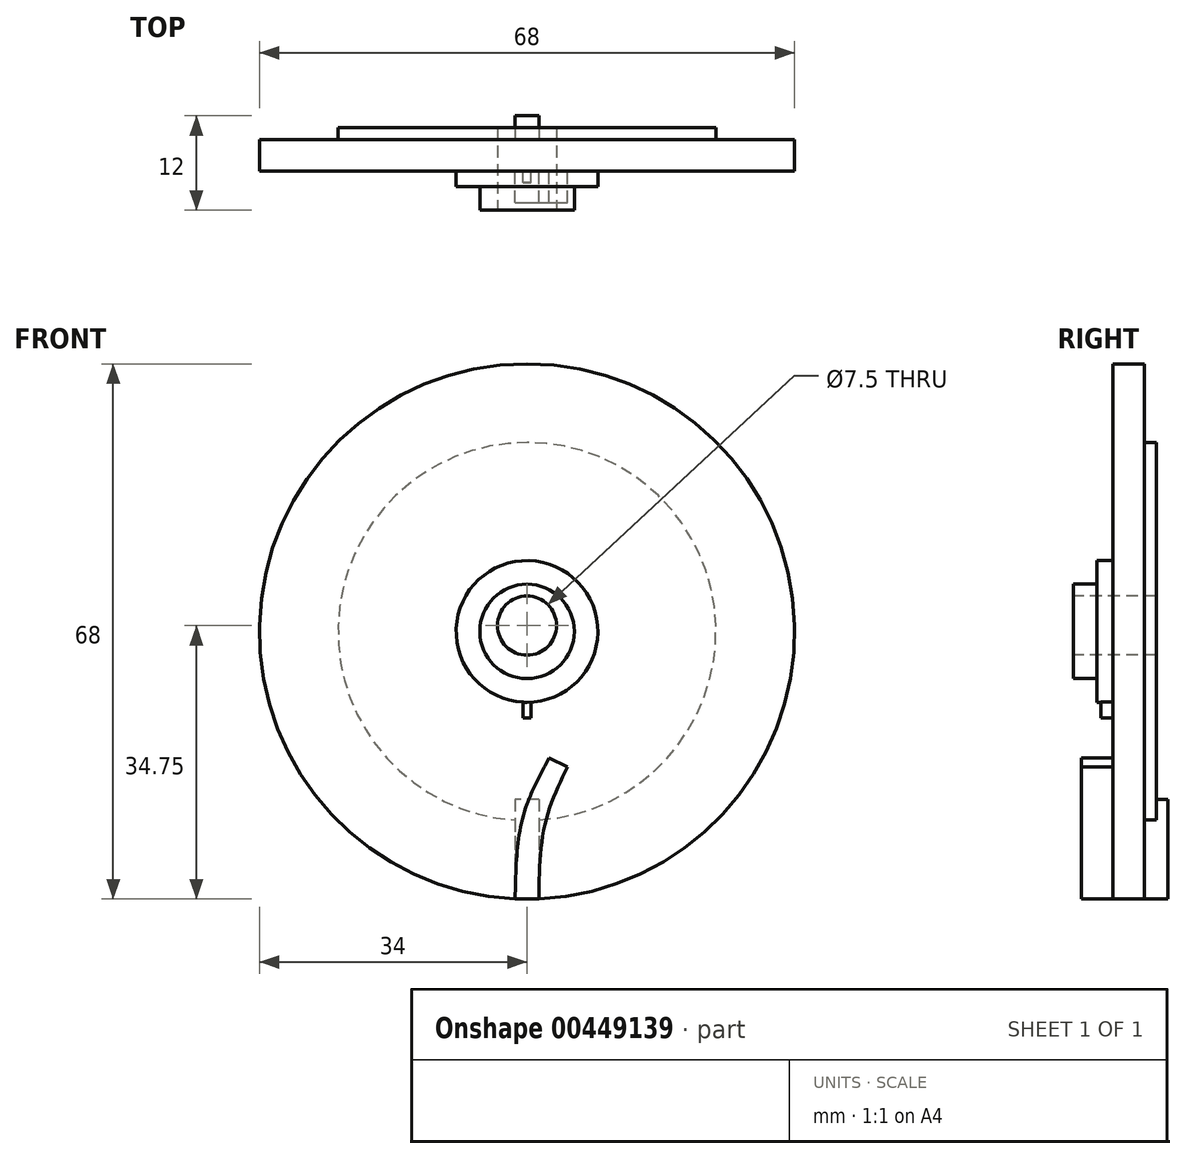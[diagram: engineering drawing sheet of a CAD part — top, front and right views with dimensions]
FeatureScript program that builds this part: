
annotation { "Feature Type Name" : "Feature", "Feature Type Description" : "" }
export const myFeature = defineFeature(function(context is Context, id is Id, definition is map)
    precondition{}
    {
        {
            var Q0;
            Q0=qCreatedBy(makeId("Front.planeOp"),FACE);
            var sketch = newSketch(context, id + "F0", { "sketchPlane" : qUnion([Q0])});
            skCircle(sketch, "E0", {"center": v(0, 0) * mm, "radius": 34 * mm});
            skSolve(sketch);
        }
        {
            var Q0;
            Q0=makeQuery(id+"F0.imprint","IMPRINT",FACE,{"disambiguationData":[TD([[makeQuery(id+"F0.imprint","IMPRINT",EDGE,{"derivedFrom":sQuery(id+"F0.wireOp",EDGE,"E0")}),1.0]])]});
            extrude(context, id + "F1", {"entities" : qUnion([Q0]), "depth" : 4 * mm});
        }
        {
            var Q0;
            Q0=qCreatedBy(makeId("Front.planeOp"),FACE);
            var sketch = newSketch(context, id + "F2", { "sketchPlane" : qUnion([Q0])});
            skCircle(sketch, "E1", {"center": v(0, 0) * mm, "radius": 6 * mm});
            skSolve(sketch);
        }
        {
            var Q0;
            Q0=qCreatedBy(makeId("Front.planeOp"),FACE);
            var sketch = newSketch(context, id + "F3", { "sketchPlane" : qUnion([Q0])});
            skCircle(sketch, "E2", {"center": v(0, 0) * mm, "radius": 24 * mm});
            skSolve(sketch);
        }
        {
            var Q0;
            Q0=qCreatedBy(makeId("Front.planeOp"),FACE);
            var sketch = newSketch(context, id + "F4", { "sketchPlane" : qUnion([Q0])});
            skCircle(sketch, "E3", {"center": v(0, 0) * mm, "radius": 9 * mm});
            skSolve(sketch);
        }
        {
            var Q0;
            Q0=qCreatedBy(makeId("Front.planeOp"),FACE);
            var sketch = newSketch(context, id + "F5", { "sketchPlane" : qUnion([Q0])});
            skLineSegment(sketch, "E4.bottom", {"start": v(1.53, -21.36) * mm, "end": v(-1.53, -21.36) * mm});
            skLineSegment(sketch, "E4.left", {"start": v(1.53, -21.36) * mm, "end": v(1.53, -33.97) * mm});
            skLineSegment(sketch, "E4.right", {"start": v(-1.53, -21.36) * mm, "end": v(-1.53, -33.97) * mm});
            skPoint(sketch, "E4.middle", {"position": v(0, -34) * mm});
            skArc(sketch, "E5", {"start": v(-1.53, -33.97) * mm, "mid": v(0, -34) * mm, "end": v(1.53, -33.97) * mm});
            skPoint(sketch, "E4.top.end.orphan", {"position": v(-1.53, -46.64) * mm});
            skPoint(sketch, "E4.top.start.orphan", {"position": v(1.53, -46.64) * mm});
            skSolve(sketch);
        }
        {
            var Q0;
            Q0 = qSketchRegion(id + "F2", true);
            extrude(context, id + "F6", {"entities" : qUnion([Q0]), "operationType" : NewBodyOperationType.ADD, "depth" : 9 * mm});
        }
        {
            var Q0;
            Q0 = qSketchRegion(id + "F4", true);
            extrude(context, id + "F7", {"entities" : qUnion([Q0]), "operationType" : NewBodyOperationType.ADD, "depth" : 6 * mm});
        }
        {
            var Q0;
            Q0 = qSketchRegion(id + "F3", true);
            extrude(context, id + "F8", {"entities" : qUnion([Q0]), "operationType" : NewBodyOperationType.ADD, "oppositeDirection" : true, "depth" : 1.5 * mm});
        }
        {
            var Q0;
            Q0 = qSketchRegion(id + "F5", true);
            extrude(context, id + "F9", {"entities" : qUnion([Q0]), "operationType" : NewBodyOperationType.ADD, "oppositeDirection" : true, "depth" : 3 * mm});
        }
        {
            var Q0;
            Q0=qCreatedBy(makeId("Right.planeOp"),FACE);
            var sketch = newSketch(context, id + "F10", { "sketchPlane" : qUnion([Q0])});
            skLineSegment(sketch, "E6", {"start": v(0, 0) * mm, "end": v(30, 0) * mm});
            skSolve(sketch);
        }
        {
            var Q0;
            Q0=qCreatedBy(makeId("Front.planeOp"),FACE);
            var sketch = newSketch(context, id + "F11", { "sketchPlane" : qUnion([Q0])});
            skLineSegment(sketch, "E7", {"start": v(0, 0) * mm, "end": v(0, 0.75) * mm});
            skCircle(sketch, "E8", {"center": v(0, 0.75) * mm, "radius": 3.75 * mm});
            skSolve(sketch);
        }
        {
            var Q0;
            Q0 = qSketchRegion(id + "F11", true);
            extrude(context, id + "F12", {"entities" : qUnion([Q0]), "operationType" : NewBodyOperationType.REMOVE, "endBound" : BoundingType.THROUGH_ALL, "oppositeDirection" : true, "depth" : 25 * mm});
        }
        {
            var Q0;
            Q0 = qSketchRegion(id + "F11", true);
            extrude(context, id + "F13", {"entities" : qUnion([Q0]), "operationType" : NewBodyOperationType.REMOVE, "endBound" : BoundingType.THROUGH_ALL, "depth" : 25 * mm});
        }
        {
            var Q0;
            Q0=qCreatedBy(makeId("Front.planeOp"),FACE);
            var sketch = newSketch(context, id + "F14", { "sketchPlane" : qUnion([Q0])});
            skLineSegment(sketch, "E9.bottom", {"start": v(0.5, -7) * mm, "end": v(-0.5, -7) * mm});
            skLineSegment(sketch, "E9.top", {"start": v(0.5, -11) * mm, "end": v(-0.5, -11) * mm});
            skLineSegment(sketch, "E9.left", {"start": v(0.5, -7) * mm, "end": v(0.5, -11) * mm});
            skLineSegment(sketch, "E9.right", {"start": v(-0.5, -7) * mm, "end": v(-0.5, -11) * mm});
            skPoint(sketch, "E9.middle", {"position": v(0, -9) * mm});
            skSolve(sketch);
        }
        {
            var Q0;
            Q0 = qSketchRegion(id + "F14", true);
            extrude(context, id + "F15", {"entities" : qUnion([Q0]), "operationType" : NewBodyOperationType.ADD, "depth" : 5.5 * mm});
        }
        {
            var Q0;
            Q0=qCreatedBy(makeId("Front.planeOp"),FACE);
            var sketch = newSketch(context, id + "F16", { "sketchPlane" : qUnion([Q0])});
            skLineSegment(sketch, "E10", {"start": v(0, 0) * mm, "end": v(0, -34) * mm});
            skArc(sketch, "E11", {"start": v(-1.5, -33.97) * mm, "mid": v(0, -34) * mm, "end": v(1.5, -33.97) * mm});
            skPoint(sketch, "E12.middle", {"position": v(0, -34) * mm});
            skPoint(sketch, "E13.1.internal.snap0", {"position": v(-0.75, -34) * mm});
            skFitSpline(sketch, "E14", {"points": [v(-1.5, -34) * mm, v(-0.58, -23.8) * mm, v(2.82, -16.06) * mm], "startDerivative": vector(0.34, 20.3) * mm, "endDerivative": vector(8.43, 15.5) * mm});
            skFitSpline(sketch, "E15", {"points": [v(1.5, -34) * mm, v(2.28, -24.5) * mm, v(5.14, -17.2) * mm], "startDerivative": vector(0.3, 18.84) * mm, "endDerivative": vector(7.1, 14.7) * mm});
            skLineSegment(sketch, "E16", {"start": v(2.82, -16.06) * mm, "end": v(5.14, -17.2) * mm});
            skSolve(sketch);
        }
        {
            var Q0;
            Q0 = qSketchRegion(id + "F16", true);
            extrude(context, id + "F17", {"entities" : qUnion([Q0]), "operationType" : NewBodyOperationType.ADD, "depth" : 8 * mm});
        }
    });
